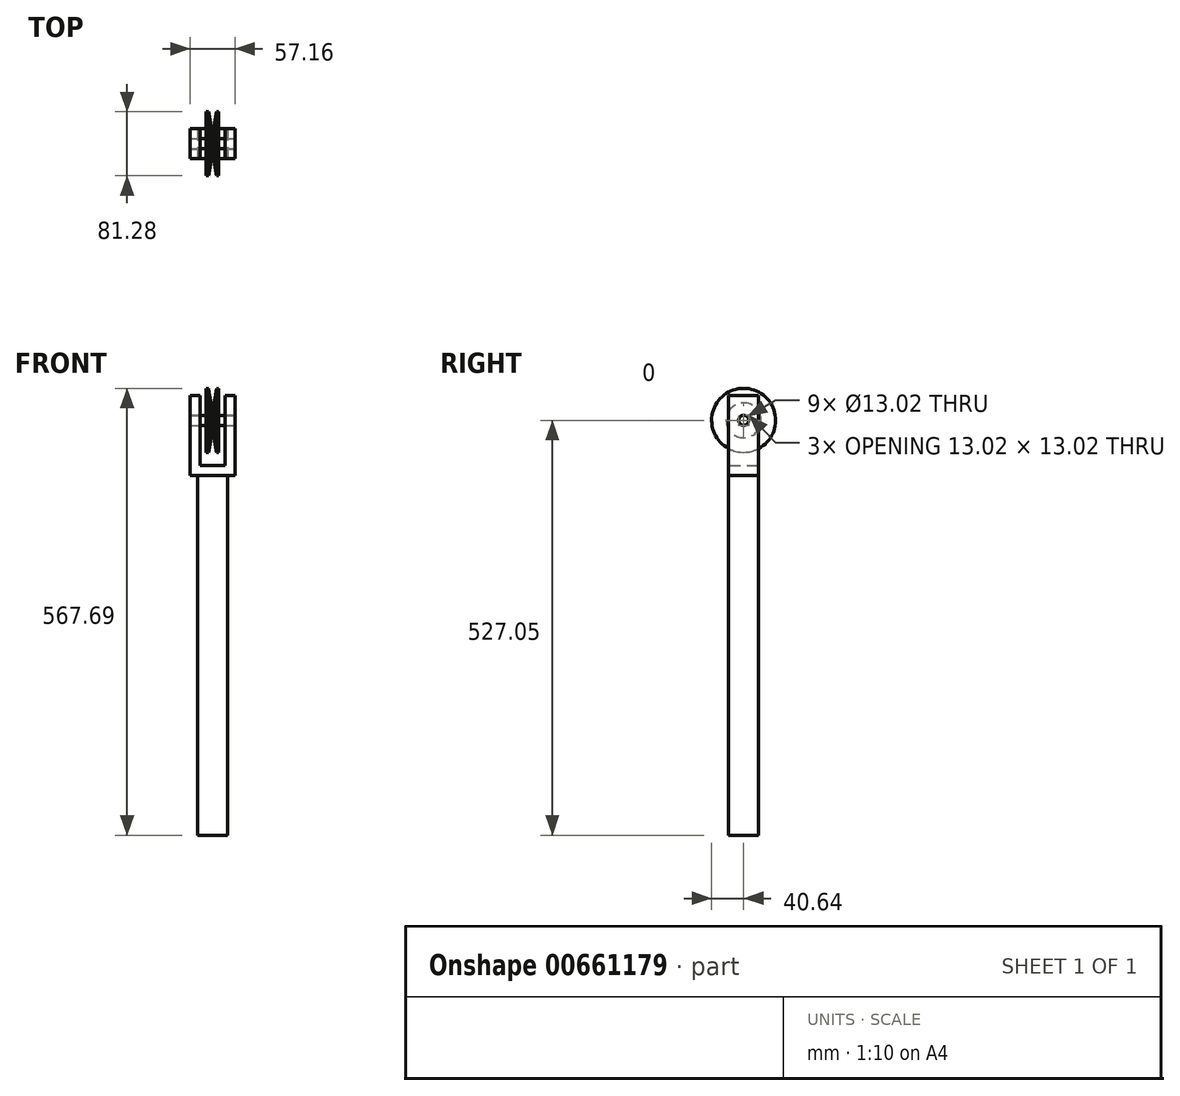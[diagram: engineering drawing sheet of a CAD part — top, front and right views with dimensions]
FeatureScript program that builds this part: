
annotation { "Feature Type Name" : "Feature", "Feature Type Description" : "" }
export const myFeature = defineFeature(function(context is Context, id is Id, definition is map)
    precondition{}
    {
        {
            var Q0;
            Q0=qCreatedBy(makeId("Front.planeOp"),FACE);
            var sketch = newSketch(context, id + "F0", { "sketchPlane" : qUnion([Q0])});
            skLineSegment(sketch, "E0", {"start": v(0, 22.22) * mm, "end": v(1.98, 22.22) * mm});
            skLineSegment(sketch, "E1", {"start": v(1.98, 22.22) * mm, "end": v(5.23, 40.64) * mm});
            skLineSegment(sketch, "E2", {"start": v(5.23, 40.64) * mm, "end": v(7.94, 40.64) * mm});
            skLineSegment(sketch, "E3", {"start": v(7.94, 40.64) * mm, "end": v(7.94, 6.35) * mm});
            skLineSegment(sketch, "E4", {"start": v(7.94, 6.35) * mm, "end": v(0, 6.35) * mm});
            skLineSegment(sketch, "E5", {"start": v(0, 6.35) * mm, "end": v(0, 22.22) * mm});
            skLineSegment(sketch, "E6.MirrorCS", {"start": v(0, 22.22) * mm, "end": v(-1.98, 22.22) * mm});
            skLineSegment(sketch, "E7.MirrorCS", {"start": v(-1.98, 22.22) * mm, "end": v(-5.23, 40.64) * mm});
            skLineSegment(sketch, "E8.MirrorCS", {"start": v(-5.23, 40.64) * mm, "end": v(-7.94, 40.64) * mm});
            skLineSegment(sketch, "E9.MirrorCS", {"start": v(-7.94, 6.35) * mm, "end": v(0, 6.35) * mm});
            skLineSegment(sketch, "E10.MirrorCS", {"start": v(-7.94, 40.64) * mm, "end": v(-7.94, 6.35) * mm});
            skLineSegment(sketch, "E11", {"start": v(-7.94, 0) * mm, "end": v(7.94, 0) * mm, "construction": true});
            skSolve(sketch);
        }
        {
            var Q0;
            Q0=makeQuery(id+"F0.imprint","IMPRINT",FACE,{"disambiguationData":[TD([[makeQuery(id+"F0.imprint","IMPRINT",EDGE,{"derivedFrom":sQuery(id+"F0.wireOp",EDGE,"E5")}),1.0]])]});
            var Q1;
            Q1=makeQuery(id+"F0.imprint","IMPRINT",FACE,{"disambiguationData":[TD([[makeQuery(id+"F0.imprint","IMPRINT",EDGE,{"derivedFrom":sQuery(id+"F0.wireOp",EDGE,"E0")}),-1.0]])]});
            var Q2;
            Q2=sQuery(id+"F0.wireOp",EDGE,"E8.MirrorCS");
            var Q3;
            Q3=sQuery(id+"F0.wireOp",EDGE,"E7.MirrorCS");
            var Q4;
            Q4=sQuery(id+"F0.wireOp",EDGE,"E6.MirrorCS");
            var Q5;
            Q5=sQuery(id+"F0.wireOp",EDGE,"E10.MirrorCS");
            var Q6;
            Q6=sQuery(id+"F0.wireOp",EDGE,"E9.MirrorCS");
            var Q7;
            Q7=sQuery(id+"F0.wireOp",EDGE,"E5");
            var Q8;
            Q8=sQuery(id+"F0.wireOp",EDGE,"E4");
            var Q9;
            Q9=sQuery(id+"F0.wireOp",EDGE,"E3");
            var Q10;
            Q10=sQuery(id+"F0.wireOp",EDGE,"E2");
            var Q11;
            Q11=sQuery(id+"F0.wireOp",EDGE,"E1");
            var Q12;
            Q12=sQuery(id+"F0.wireOp",EDGE,"E0");
            var Q13;
            Q13=sQuery(id+"F0.wireOp",EDGE,"E11");
            revolve(context, id + "F1", {"entities" : qUnion([Q0, Q1]), "surfaceEntities" : qUnion([Q2, Q3, Q4, Q5, Q6, Q7, Q8, Q9, Q10, Q11, Q12]), "axis" : qUnion([Q13]), "revolveType" : RevolveType.FULL});
        }
        {
            var Q0;
            Q0=qCreatedBy(makeId("Front.planeOp"),FACE);
            var sketch = newSketch(context, id + "F2", { "sketchPlane" : qUnion([Q0])});
            skLineSegment(sketch, "E12", {"start": v(28.57, 31.75) * mm, "end": v(15.87, 31.75) * mm});
            skLineSegment(sketch, "E13", {"start": v(15.87, 31.75) * mm, "end": v(15.88, -57.15) * mm});
            skLineSegment(sketch, "E14", {"start": v(15.88, -57.15) * mm, "end": v(-15.88, -57.15) * mm});
            skLineSegment(sketch, "E15", {"start": v(-15.88, -57.15) * mm, "end": v(-15.87, 31.75) * mm});
            skLineSegment(sketch, "E16", {"start": v(-15.87, 31.75) * mm, "end": v(-28.57, 31.75) * mm});
            skLineSegment(sketch, "E17", {"start": v(-28.57, 31.75) * mm, "end": v(-28.57, -69.85) * mm});
            skLineSegment(sketch, "E18", {"start": v(-28.57, -69.85) * mm, "end": v(28.57, -69.85) * mm});
            skLineSegment(sketch, "E19", {"start": v(28.57, -69.85) * mm, "end": v(28.57, 31.75) * mm});
            skLineSegment(sketch, "E20", {"start": v(0, -57.15) * mm, "end": v(0, -69.85) * mm, "construction": true});
            skSolve(sketch);
        }
        {
            var Q0;
            Q0=makeQuery(id+"F2.imprint","IMPRINT",FACE,{"disambiguationData":[TD([[makeQuery(id+"F2.imprint","IMPRINT",EDGE,{"derivedFrom":sQuery(id+"F2.wireOp",EDGE,"E12")}),1.0]])]});
            extrude(context, id + "F3", {"entities" : qUnion([Q0]), "endBound" : BoundingType.SYMMETRIC, "depth" : 38.1 * mm, "offsetDistance" : 25.4 * mm});
        }
        {
            var Q0;
            Q0=qCreatedBy(makeId("Right.planeOp"),FACE);
            var sketch = newSketch(context, id + "F4", { "sketchPlane" : qUnion([Q0])});
            skCircle(sketch, "E21", {"center": v(0, 0) * mm, "radius": 6.5 * mm});
            skSolve(sketch);
        }
        {
            var Q0;
            Q0=makeQuery(id+"F4.imprint","IMPRINT",FACE,{"disambiguationData":[TD([[makeQuery(id+"F4.imprint","IMPRINT",EDGE,{"derivedFrom":sQuery(id+"F4.wireOp",EDGE,"E21")}),1.0]])]});
            extrude(context, id + "F5", {"entities" : qUnion([Q0]), "operationType" : NewBodyOperationType.REMOVE, "endBound" : BoundingType.THROUGH_ALL, "oppositeDirection" : true, "depth" : 25.4 * mm, "offsetDistance" : 25.4 * mm, "hasSecondDirection" : true, "secondDirectionBound" : SecondDirectionBoundingType.THROUGH_ALL, "secondDirectionOppositeDirection" : false, "secondDirectionDepth" : 25.4 * mm});
        }
        {
            var Q0;
            Q0=makeQuery(id+"F3.opExtrude","SWEPT_FACE",FACE,{"disambiguationData":[OSD([sQuery(id+"F2.wireOp",EDGE,"E18")])]});
            var sketch = newSketch(context, id + "F6", { "sketchPlane" : qUnion([Q0])});
            skLineSegment(sketch, "E22.bottom", {"start": v(-19.05, -19.05) * mm, "end": v(19.05, -19.05) * mm});
            skLineSegment(sketch, "E22.top", {"start": v(-19.05, 19.05) * mm, "end": v(19.05, 19.05) * mm});
            skLineSegment(sketch, "E22.left", {"start": v(-19.05, -19.05) * mm, "end": v(-19.05, 19.05) * mm});
            skLineSegment(sketch, "E22.right", {"start": v(19.05, -19.05) * mm, "end": v(19.05, 19.05) * mm});
            skPoint(sketch, "E22.middle", {"position": v(0, 0) * mm});
            skSolve(sketch);
        }
        {
            var Q0;
            Q0=makeQuery(id+"F6.imprint","IMPRINT",FACE,{"disambiguationData":[TD([[makeQuery(id+"F6.imprint","IMPRINT",EDGE,{"derivedFrom":sQuery(id+"F6.wireOp",EDGE,"E22.bottom")}),1.0]])]});
            extrude(context, id + "F7", {"entities" : qUnion([Q0]), "depth" : 457.2 * mm, "offsetDistance" : 25.4 * mm});
        }
        {
            var Q0;
            Q0=makeQuery(id+"F3.opExtrude","SWEPT_FACE",FACE,{"disambiguationData":[OSD([sQuery(id+"F2.wireOp",EDGE,"E19")])]});
            var sketch = newSketch(context, id + "F8", { "sketchPlane" : qUnion([Q0])});
            skCircle(sketch, "E23", {"center": v(0, 0) * mm, "radius": 6.35 * mm});
            skSolve(sketch);
        }
        {
            var Q0;
            Q0=makeQuery(id+"F8.imprint","IMPRINT",FACE,{"disambiguationData":[TD([[makeQuery(id+"F8.imprint","IMPRINT",EDGE,{"derivedFrom":sQuery(id+"F8.wireOp",EDGE,"E23")}),1.0]])]});
            extrude(context, id + "F9", {"entities" : qUnion([Q0]), "operationType" : NewBodyOperationType.ADD, "oppositeDirection" : true, "depth" : 57.15 * mm, "offsetDistance" : 25.4 * mm});
        }
    });
